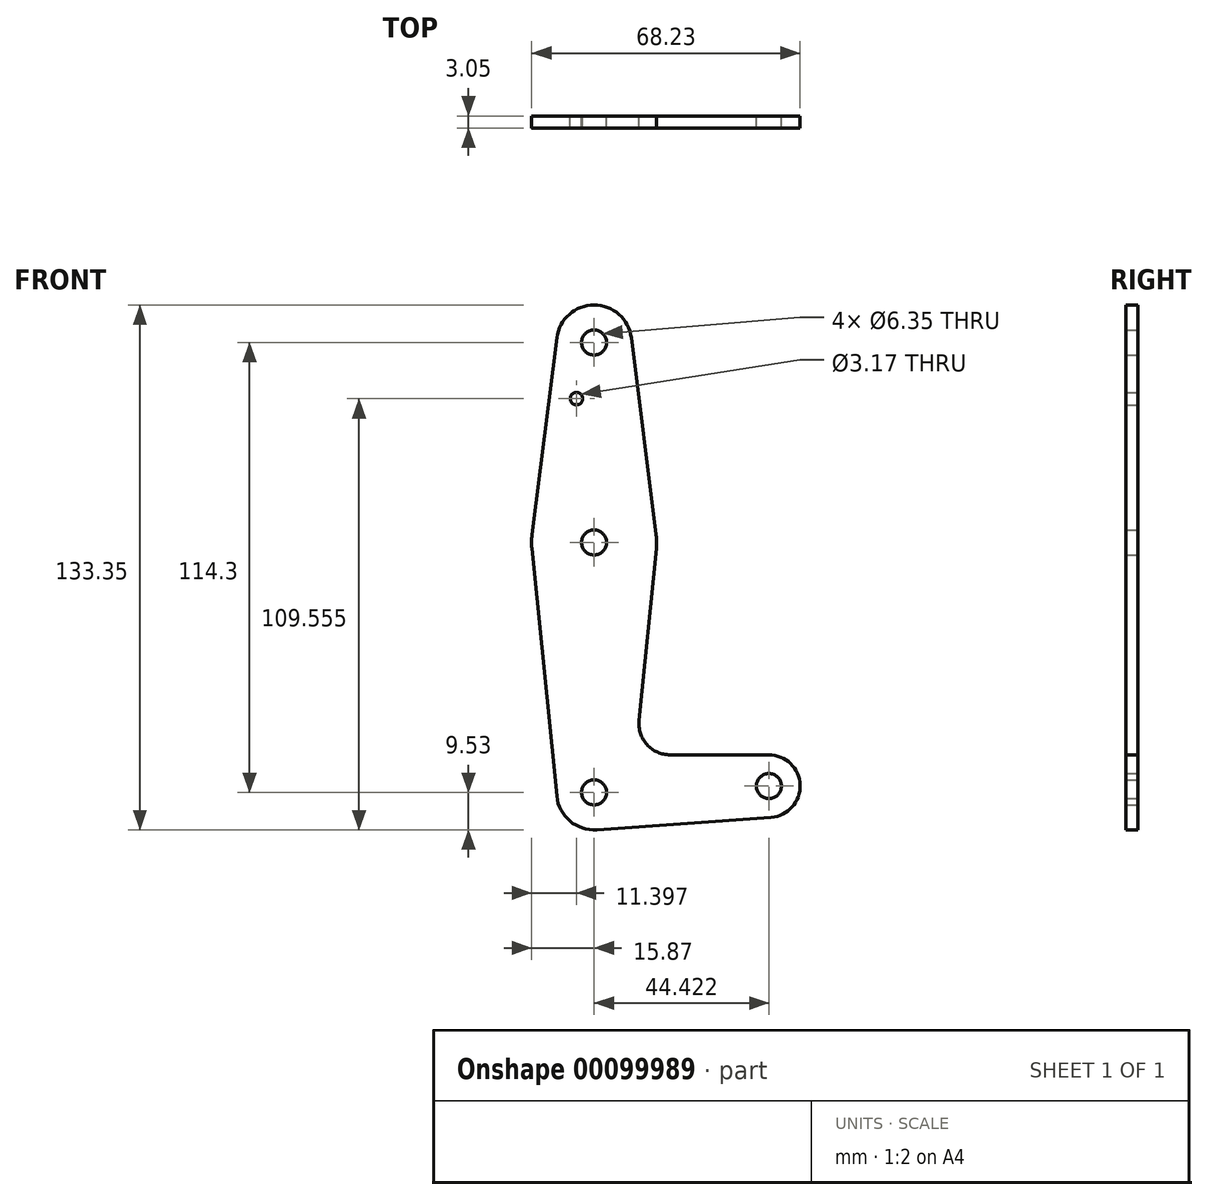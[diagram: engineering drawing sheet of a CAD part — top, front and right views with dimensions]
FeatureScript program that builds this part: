
annotation { "Feature Type Name" : "Feature", "Feature Type Description" : "" }
export const myFeature = defineFeature(function(context is Context, id is Id, definition is map)
    precondition{}
    {
        {
            var Q0;
            Q0=qCreatedBy(makeId("Front.planeOp"),FACE);
            var sketch = newSketch(context, id + "F0", { "sketchPlane" : qUnion([Q0])});
            skLineSegment(sketch, "E0", {"start": v(0, 0) * mm, "end": v(0, 50.8) * mm});
            skLineSegment(sketch, "E1", {"start": v(0, 0) * mm, "end": v(0, -63.5) * mm});
            skCircle(sketch, "E2", {"center": v(0, 50.8) * mm, "radius": 9.53 * mm});
            skCircle(sketch, "E3", {"center": v(0, 0) * mm, "radius": 15.88 * mm});
            skCircle(sketch, "E4", {"center": v(44.42, -61.91) * mm, "radius": 7.94 * mm});
            skLineSegment(sketch, "E5", {"start": v(0, -63.5) * mm, "end": v(44.42, -61.91) * mm});
            skCircle(sketch, "E6", {"center": v(0, -63.5) * mm, "radius": 9.53 * mm});
            skLineSegment(sketch, "E7", {"start": v(0, 50.8) * mm, "end": v(0, -63.5) * mm});
            skLineSegment(sketch, "E8", {"start": v(-9.45, 52) * mm, "end": v(-15.75, 1.98) * mm});
            skLineSegment(sketch, "E9", {"start": v(9.45, 52) * mm, "end": v(15.75, 1.98) * mm});
            skLineSegment(sketch, "E10", {"start": v(-15.8, -1.59) * mm, "end": v(-9.48, -64.45) * mm});
            skLineSegment(sketch, "E11", {"start": v(15.8, -1.59) * mm, "end": v(11.4, -45.23) * mm});
            skLineSegment(sketch, "E12", {"start": v(19.32, -53.97) * mm, "end": v(44.42, -53.97) * mm});
            skLineSegment(sketch, "E13", {"start": v(0.68, -73) * mm, "end": v(44.99, -69.83) * mm});
            skCircle(sketch, "E14", {"center": v(0, 50.8) * mm, "radius": 3.18 * mm});
            skCircle(sketch, "E15", {"center": v(0, 0) * mm, "radius": 3.18 * mm});
            skCircle(sketch, "E16", {"center": v(0, -63.5) * mm, "radius": 3.18 * mm});
            skCircle(sketch, "E17", {"center": v(44.42, -61.91) * mm, "radius": 3.18 * mm});
            skCircle(sketch, "E18", {"center": v(-4.47, 36.53) * mm, "radius": 1.59 * mm});
            skArc(sketch, "E19.filletArc", {"start": v(11.4, -45.23) * mm, "mid": v(13.42, -51.36) * mm, "end": v(19.32, -53.98) * mm});
            skSolve(sketch);
        }
        {
            var Q0;
            Q0 = qSketchRegion(id + "F0", true);
            var Q1;
            {var subQ0=sQuery(id+"F0.wireOp",EDGE,"E16");var subQ1=sQuery(id+"F0.wireOp",EDGE,"E5");var subQ2=makeQuery(id+"F0.imprint","INTERSECT",VERTEX,{"derivedFrom":[subQ1,subQ0]});Q1=makeQuery(id+"F0.imprint","IMPRINT",FACE,{"disambiguationData":[TD([[makeQuery(id+"F0.imprint","IMPRINT",EDGE,{"disambiguationData":[TD([[subQ2,-1.0]])],"derivedFrom":subQ1}),1.0]])]});}
            extrude(context, id + "F1", {"entities" : qUnion([Q0, Q1]), "depth" : 3.05 * mm});
        }
    });
